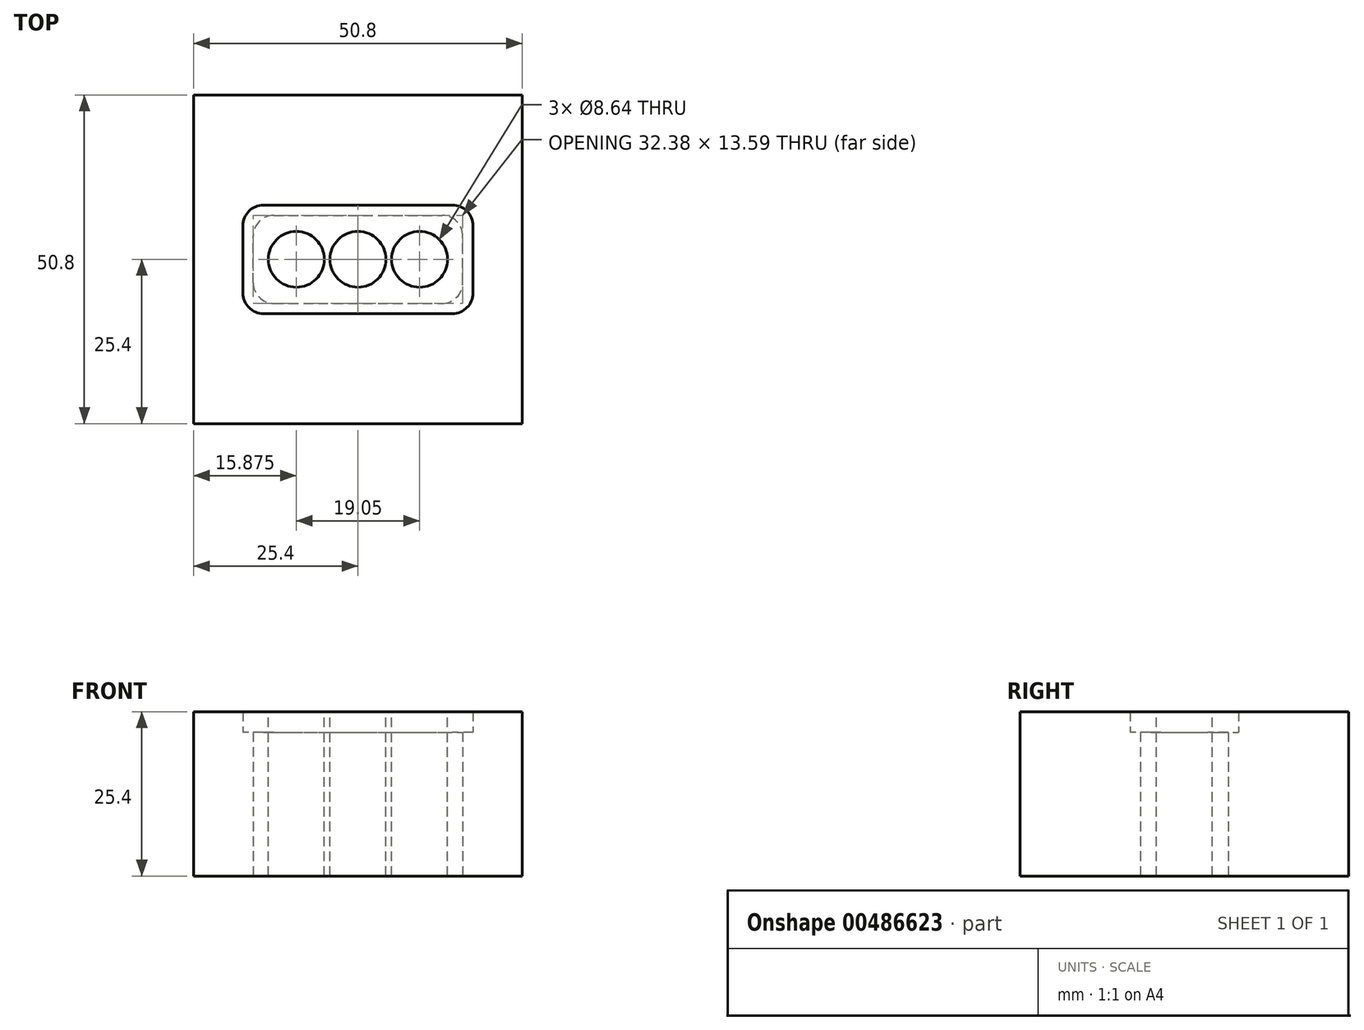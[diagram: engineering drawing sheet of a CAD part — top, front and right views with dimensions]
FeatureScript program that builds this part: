
annotation { "Feature Type Name" : "Feature", "Feature Type Description" : "" }
export const myFeature = defineFeature(function(context is Context, id is Id, definition is map)
    precondition{}
    {
        {
            var Q0;
            Q0=qCreatedBy(makeId("Top.planeOp"),FACE);
            var sketch = newSketch(context, id + "F0", { "sketchPlane" : qUnion([Q0])});
            skLineSegment(sketch, "E0.bottom", {"start": v(25.4, -25.4) * mm, "end": v(-25.4, -25.4) * mm});
            skLineSegment(sketch, "E0.top", {"start": v(25.4, 25.4) * mm, "end": v(-25.4, 25.4) * mm});
            skLineSegment(sketch, "E0.left", {"start": v(25.4, -25.4) * mm, "end": v(25.4, 25.4) * mm});
            skLineSegment(sketch, "E0.right", {"start": v(-25.4, -25.4) * mm, "end": v(-25.4, 25.4) * mm});
            skPoint(sketch, "E0.middle", {"position": v(0, 0) * mm});
            skLineSegment(sketch, "E1.bottom", {"start": v(-14.6, -8.38) * mm, "end": v(14.6, -8.38) * mm});
            skLineSegment(sketch, "E1.top", {"start": v(-14.6, 8.38) * mm, "end": v(14.6, 8.38) * mm});
            skLineSegment(sketch, "E1.left", {"start": v(-17.78, -5.2) * mm, "end": v(-17.78, 5.2) * mm});
            skLineSegment(sketch, "E1.right", {"start": v(17.78, -5.2) * mm, "end": v(17.78, 5.2) * mm});
            skPoint(sketch, "E2.visualSharp", {"position": v(-17.78, 8.38) * mm});
            skArc(sketch, "E2.filletArc", {"start": v(-14.6, 8.38) * mm, "mid": v(-16.85, 7.45) * mm, "end": v(-17.78, 5.2) * mm});
            skPoint(sketch, "E3.visualSharp", {"position": v(17.78, 8.38) * mm});
            skArc(sketch, "E3.filletArc", {"start": v(17.78, 5.2) * mm, "mid": v(16.85, 7.45) * mm, "end": v(14.6, 8.38) * mm});
            skPoint(sketch, "E4.visualSharp", {"position": v(17.78, -8.38) * mm});
            skArc(sketch, "E4.filletArc", {"start": v(14.6, -8.38) * mm, "mid": v(16.85, -7.45) * mm, "end": v(17.78, -5.2) * mm});
            skPoint(sketch, "E5.visualSharp", {"position": v(-17.78, -8.38) * mm});
            skArc(sketch, "E5.filletArc", {"start": v(-17.78, -5.2) * mm, "mid": v(-16.85, -7.45) * mm, "end": v(-14.6, -8.38) * mm});
            skLineSegment(sketch, "E6.bottom", {"start": v(-13.02, -6.8) * mm, "end": v(13.02, -6.8) * mm});
            skLineSegment(sketch, "E6.top", {"start": v(-13.02, 6.8) * mm, "end": v(13.02, 6.8) * mm});
            skLineSegment(sketch, "E6.left", {"start": v(-16.2, -3.62) * mm, "end": v(-16.2, 3.62) * mm});
            skLineSegment(sketch, "E6.right", {"start": v(16.2, -3.62) * mm, "end": v(16.2, 3.62) * mm});
            skPoint(sketch, "E7.visualSharp", {"position": v(-16.2, 6.8) * mm});
            skArc(sketch, "E7.filletArc", {"start": v(-13.02, 6.8) * mm, "mid": v(-15.26, 5.86) * mm, "end": v(-16.2, 3.62) * mm});
            skPoint(sketch, "E8.visualSharp", {"position": v(-16.2, -6.8) * mm});
            skArc(sketch, "E8.filletArc", {"start": v(-16.2, -3.62) * mm, "mid": v(-15.26, -5.86) * mm, "end": v(-13.02, -6.8) * mm});
            skPoint(sketch, "E9.visualSharp", {"position": v(16.2, 6.8) * mm});
            skArc(sketch, "E9.filletArc", {"start": v(16.2, 3.62) * mm, "mid": v(15.26, 5.86) * mm, "end": v(13.02, 6.8) * mm});
            skPoint(sketch, "E10.visualSharp", {"position": v(16.2, -6.8) * mm});
            skArc(sketch, "E10.filletArc", {"start": v(13.02, -6.8) * mm, "mid": v(15.26, -5.86) * mm, "end": v(16.2, -3.62) * mm});
            skSolve(sketch);
        }
        {
            var Q0;
            Q0=makeQuery(id+"F0.imprint","IMPRINT",FACE,{"disambiguationData":[TD([[makeQuery(id+"F0.imprint","IMPRINT",EDGE,{"derivedFrom":sQuery(id+"F0.wireOp",EDGE,"E0.bottom")}),-1.0]])]});
            extrude(context, id + "F1", {"entities" : qUnion([Q0]), "depth" : 25.4 * mm, "offsetDistance" : 25.4 * mm});
        }
        {
            var Q0;
            Q0=makeQuery(id+"F0.imprint","IMPRINT",FACE,{"disambiguationData":[TD([[makeQuery(id+"F0.imprint","IMPRINT",EDGE,{"derivedFrom":sQuery(id+"F0.wireOp",EDGE,"E1.bottom")}),1.0]])]});
            extrude(context, id + "F2", {"entities" : qUnion([Q0]), "operationType" : NewBodyOperationType.ADD, "depth" : 22.22 * mm, "offsetDistance" : 25.4 * mm});
        }
        {
            var Q0;
            Q0=makeQuery(id+"F0.imprint","IMPRINT",FACE,{"disambiguationData":[TD([[makeQuery(id+"F0.imprint","IMPRINT",EDGE,{"derivedFrom":sQuery(id+"F0.wireOp",EDGE,"E6.bottom")}),1.0]])]});
            extrude(context, id + "F3", {"entities" : qUnion([Q0]), "depth" : 25.4 * mm, "offsetDistance" : 25.4 * mm});
        }
        {
            var Q0;
            Q0=makeQuery(id+"F2.opExtrude","CAP_FACE",FACE,{"disambiguationData":[OSD([sQuery(id+"F0.wireOp",EDGE,"E1.bottom"),sQuery(id+"F0.wireOp",EDGE,"E1.top"),sQuery(id+"F0.wireOp",EDGE,"E1.left"),sQuery(id+"F0.wireOp",EDGE,"E1.right"),sQuery(id+"F0.wireOp",EDGE,"E2.filletArc"),sQuery(id+"F0.wireOp",EDGE,"E3.filletArc"),sQuery(id+"F0.wireOp",EDGE,"E4.filletArc"),sQuery(id+"F0.wireOp",EDGE,"E5.filletArc"),sQuery(id+"F0.wireOp",EDGE,"E6.bottom"),sQuery(id+"F0.wireOp",EDGE,"E6.top"),sQuery(id+"F0.wireOp",EDGE,"E6.left"),sQuery(id+"F0.wireOp",EDGE,"E6.right"),sQuery(id+"F0.wireOp",EDGE,"E7.filletArc"),sQuery(id+"F0.wireOp",EDGE,"E8.filletArc"),sQuery(id+"F0.wireOp",EDGE,"E9.filletArc"),sQuery(id+"F0.wireOp",EDGE,"E10.filletArc")])],"isStart":false});
            extrude(context, id + "F4", {"entities" : qUnion([Q0]), "depth" : 3.17 * mm, "offsetDistance" : 25.4 * mm});
        }
        {
            var Q0;
            Q0=makeQuery(id+"F3.opExtrude","SWEPT_BODY",BODY,{"disambiguationData":[OSD([sQuery(id+"F0.wireOp",EDGE,"E6.bottom"),sQuery(id+"F0.wireOp",EDGE,"E6.top"),sQuery(id+"F0.wireOp",EDGE,"E6.left"),sQuery(id+"F0.wireOp",EDGE,"E6.right"),sQuery(id+"F0.wireOp",EDGE,"E7.filletArc"),sQuery(id+"F0.wireOp",EDGE,"E8.filletArc"),sQuery(id+"F0.wireOp",EDGE,"E9.filletArc"),sQuery(id+"F0.wireOp",EDGE,"E10.filletArc")])]});
            var Q1;
            Q1=makeQuery(id+"F4.opExtrude","SWEPT_BODY",BODY,{"disambiguationData":[OSD([sQuery(id+"F0.wireOp",EDGE,"E1.bottom"),sQuery(id+"F0.wireOp",EDGE,"E1.top"),sQuery(id+"F0.wireOp",EDGE,"E1.left"),sQuery(id+"F0.wireOp",EDGE,"E1.right"),sQuery(id+"F0.wireOp",EDGE,"E2.filletArc"),sQuery(id+"F0.wireOp",EDGE,"E3.filletArc"),sQuery(id+"F0.wireOp",EDGE,"E4.filletArc"),sQuery(id+"F0.wireOp",EDGE,"E5.filletArc"),sQuery(id+"F0.wireOp",EDGE,"E6.bottom"),sQuery(id+"F0.wireOp",EDGE,"E6.top"),sQuery(id+"F0.wireOp",EDGE,"E6.left"),sQuery(id+"F0.wireOp",EDGE,"E6.right"),sQuery(id+"F0.wireOp",EDGE,"E7.filletArc"),sQuery(id+"F0.wireOp",EDGE,"E8.filletArc"),sQuery(id+"F0.wireOp",EDGE,"E9.filletArc"),sQuery(id+"F0.wireOp",EDGE,"E10.filletArc")])]});
            booleanBodies(context, id + "F5", {"operationType" : BooleanOperationType.UNION, "tools" : qUnion([Q0, Q1])});
        }
        {
            var Q0;
            {var subQ0=sQuery(id+"F0.wireOp",EDGE,"E10.filletArc");var subQ1=sQuery(id+"F0.wireOp",EDGE,"E9.filletArc");var subQ2=sQuery(id+"F0.wireOp",EDGE,"E8.filletArc");var subQ3=sQuery(id+"F0.wireOp",EDGE,"E7.filletArc");var subQ4=sQuery(id+"F0.wireOp",EDGE,"E6.right");var subQ5=sQuery(id+"F0.wireOp",EDGE,"E6.left");var subQ6=sQuery(id+"F0.wireOp",EDGE,"E6.top");var subQ7=sQuery(id+"F0.wireOp",EDGE,"E6.bottom");Q0=makeQuery(id+"F5.opBoolean","MERGE",FACE,{"derivedFrom":[makeQuery(id+"F3.opExtrude","CAP_FACE",FACE,{"disambiguationData":[OSD([subQ7,subQ6,subQ5,subQ4,subQ3,subQ2,subQ1,subQ0])],"isStart":false}),makeQuery(id+"F4.opExtrude","CAP_FACE",FACE,{"disambiguationData":[OSD([sQuery(id+"F0.wireOp",EDGE,"E1.bottom"),sQuery(id+"F0.wireOp",EDGE,"E1.top"),sQuery(id+"F0.wireOp",EDGE,"E1.left"),sQuery(id+"F0.wireOp",EDGE,"E1.right"),sQuery(id+"F0.wireOp",EDGE,"E2.filletArc"),sQuery(id+"F0.wireOp",EDGE,"E3.filletArc"),sQuery(id+"F0.wireOp",EDGE,"E4.filletArc"),sQuery(id+"F0.wireOp",EDGE,"E5.filletArc"),subQ7,subQ6,subQ5,subQ4,subQ3,subQ2,subQ1,subQ0])],"isStart":false})]});}
            var sketch = newSketch(context, id + "F6", { "sketchPlane" : qUnion([Q0])});
            skCircle(sketch, "E11", {"center": v(0, 0) * mm, "radius": 4.32 * mm});
            skCircle(sketch, "E12", {"center": v(-9.53, 0) * mm, "radius": 4.32 * mm});
            skCircle(sketch, "E13", {"center": v(9.53, 0) * mm, "radius": 4.32 * mm});
            skSolve(sketch);
        }
        {
            var Q0;
            Q0 = qSketchRegion(id + "F6", true);
            extrude(context, id + "F7", {"entities" : qUnion([Q0]), "operationType" : NewBodyOperationType.REMOVE, "oppositeDirection" : true, "depth" : 25.4 * mm, "offsetDistance" : 25.4 * mm});
        }
    });
